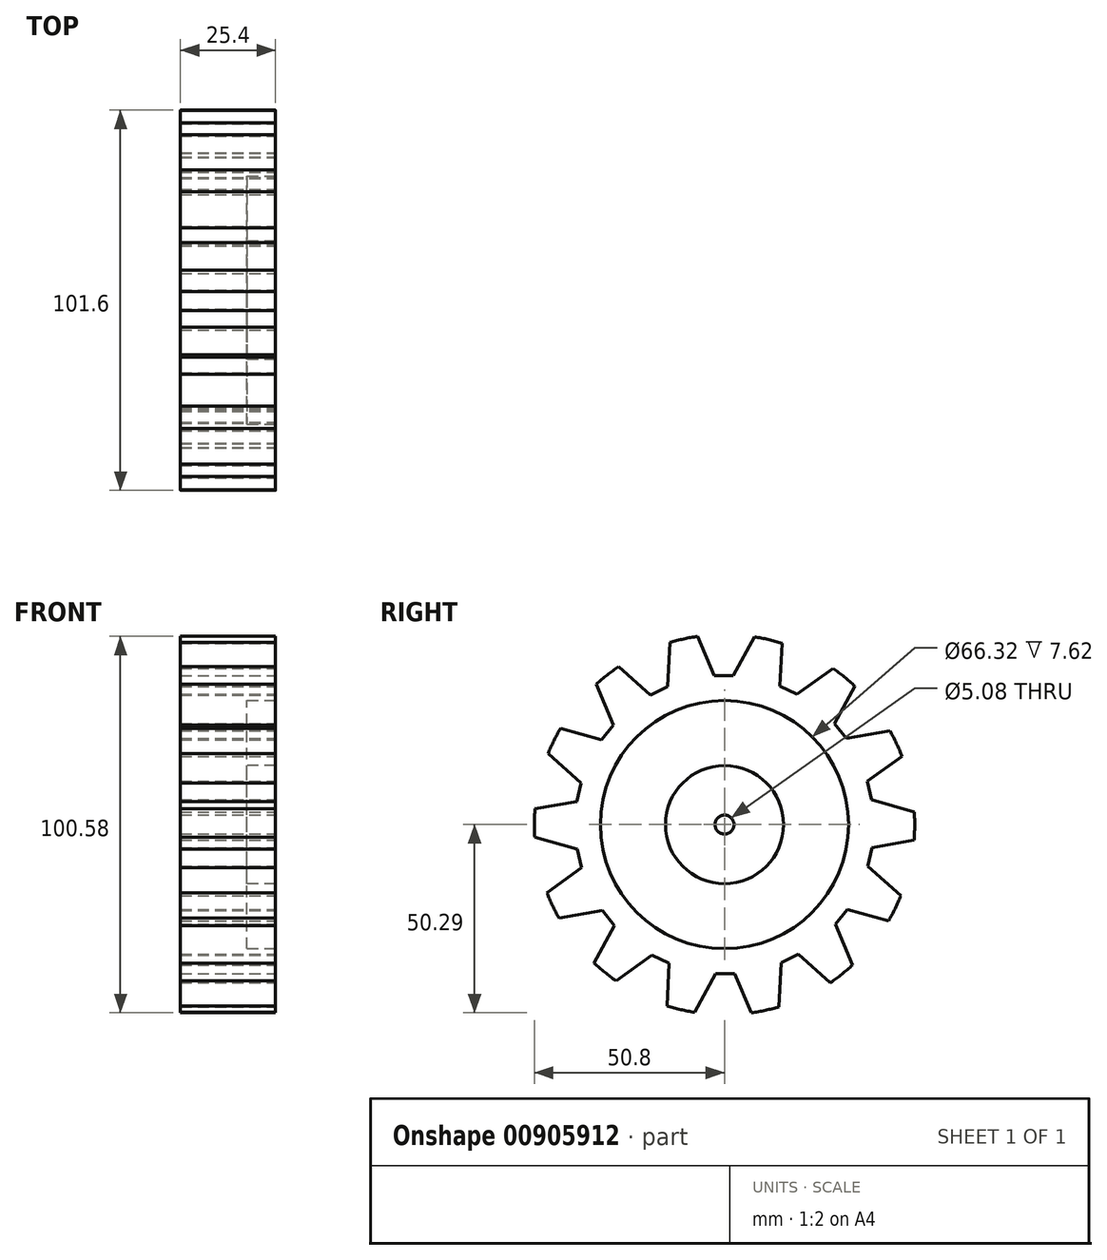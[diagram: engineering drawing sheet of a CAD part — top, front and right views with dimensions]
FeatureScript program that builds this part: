
annotation { "Feature Type Name" : "Feature", "Feature Type Description" : "" }
export const myFeature = defineFeature(function(context is Context, id is Id, definition is map)
    precondition{}
    {
        {
            var Q0;
            Q0=qCreatedBy(makeId("Right.planeOp"),FACE);
            var sketch = newSketch(context, id + "F0", { "sketchPlane" : qUnion([Q0])});
            skCircle(sketch, "E0", {"center": v(0, 0) * mm, "radius": 50.8 * mm});
            skSolve(sketch);
        }
        {
            var Q0;
            Q0 = qSketchRegion(id + "F0", true);
            extrude(context, id + "F1", {"entities" : qUnion([Q0]), "depth" : 25.4 * mm, "offsetDistance" : 25.4 * mm});
        }
        {
            var Q0;
            Q0=makeQuery(id+"F1.opExtrude","CAP_FACE",FACE,{"disambiguationData":[OSD([sQuery(id+"F0.wireOp",EDGE,"E0")])],"isStart":false});
            var sketch = newSketch(context, id + "F2", { "sketchPlane" : qUnion([Q0])});
            skLineSegment(sketch, "E1", {"start": v(8, 50.17) * mm, "end": v(2.32, 39.78) * mm});
            skLineSegment(sketch, "E2", {"start": v(2.32, 39.78) * mm, "end": v(-2.76, 39.78) * mm});
            skLineSegment(sketch, "E3", {"start": v(-2.76, 39.78) * mm, "end": v(-7.18, 50.29) * mm});
            skSolve(sketch);
        }
        {
            var Q0;
            {var subQ0=sQuery(id+"F2.wireOp",EDGE,"E1");Q0=makeQuery(id+"F2.imprint","IMPRINT",FACE,{"disambiguationData":[TD([[makeQuery(id+"F2.imprint","IMPRINT",EDGE,{"derivedFrom":subQ0}),-1.0]])]});}
            extrude(context, id + "F3", {"entities" : qUnion([Q0]), "operationType" : NewBodyOperationType.REMOVE, "oppositeDirection" : true, "depth" : 76.2 * mm, "offsetDistance" : 25.4 * mm});
        }
        {
            var Q0;
            Q0=makeQuery(id+"F3.boolean.opBoolean","COPY",FACE,{"derivedFrom":makeQuery(id+"F3.opExtrude","SWEPT_FACE",FACE,{"disambiguationData":[OSD([sQuery(id+"F2.wireOp",EDGE,"E2")])]})});
            var Q1;
            Q1=makeQuery(id+"F3.boolean.opBoolean","COPY",FACE,{"derivedFrom":makeQuery(id+"F3.opExtrude","SWEPT_FACE",FACE,{"disambiguationData":[OSD([sQuery(id+"F2.wireOp",EDGE,"E3")])]})});
            var Q2;
            Q2=makeQuery(id+"F3.boolean.opBoolean","COPY",FACE,{"derivedFrom":makeQuery(id+"F3.opExtrude","SWEPT_FACE",FACE,{"disambiguationData":[OSD([sQuery(id+"F2.wireOp",EDGE,"E1")])]})});
            var Q3;
            Q3=makeQuery(id+"F1.opExtrude","CAP_EDGE",EDGE,{"disambiguationData":[OSD([sQuery(id+"F0.wireOp",EDGE,"E0")])],"isStart":false});
            circularPattern(context, id + "F4", {"patternType" : PatternType.FACE, "faces" : qUnion([Q0, Q1, Q2]), "axis" : qUnion([Q3]), "angle" : 360 * degree, "instanceCount" : 28, "equalSpace" : true});
        }
        {
            var Q0;
            Q0=makeQuery(id+"F1.opExtrude","CAP_FACE",FACE,{"disambiguationData":[OSD([sQuery(id+"F0.wireOp",EDGE,"E0")])],"isStart":false});
            var sketch = newSketch(context, id + "F5", { "sketchPlane" : qUnion([Q0])});
            skCircle(sketch, "E4", {"center": v(0, 0) * mm, "radius": 33.16 * mm});
            skSolve(sketch);
        }
        {
            var Q0;
            Q0 = qSketchRegion(id + "F5", true);
            extrude(context, id + "F6", {"entities" : qUnion([Q0]), "operationType" : NewBodyOperationType.REMOVE, "oppositeDirection" : true, "depth" : 7.62 * mm, "offsetDistance" : 25.4 * mm});
        }
        {
            var Q0;
            Q0=makeQuery(id+"F6.boolean.opBoolean","COPY",FACE,{"derivedFrom":makeQuery(id+"F6.opExtrude","CAP_FACE",FACE,{"disambiguationData":[OSD([sQuery(id+"F5.wireOp",EDGE,"E4")])],"isStart":false})});
            var sketch = newSketch(context, id + "F7", { "sketchPlane" : qUnion([Q0])});
            skCircle(sketch, "E5", {"center": v(0, 0) * mm, "radius": 15.77 * mm});
            skSolve(sketch);
        }
        {
            var Q0;
            Q0 = qSketchRegion(id + "F7", true);
            extrude(context, id + "F8", {"entities" : qUnion([Q0]), "operationType" : NewBodyOperationType.ADD, "depth" : 7.62 * mm, "offsetDistance" : 25.4 * mm});
        }
        {
            var Q0;
            Q0=makeQuery(id+"F8.opExtrude","CAP_FACE",FACE,{"disambiguationData":[OSD([sQuery(id+"F7.wireOp",EDGE,"E5")])],"isStart":false});
            var sketch = newSketch(context, id + "F9", { "sketchPlane" : qUnion([Q0])});
            skCircle(sketch, "E6", {"center": v(0, 0) * mm, "radius": 2.54 * mm});
            skSolve(sketch);
        }
        {
            var Q0;
            Q0 = qSketchRegion(id + "F9", true);
            extrude(context, id + "F10", {"entities" : qUnion([Q0]), "operationType" : NewBodyOperationType.REMOVE, "oppositeDirection" : true, "depth" : 76.2 * mm, "offsetDistance" : 25.4 * mm});
        }
    });
